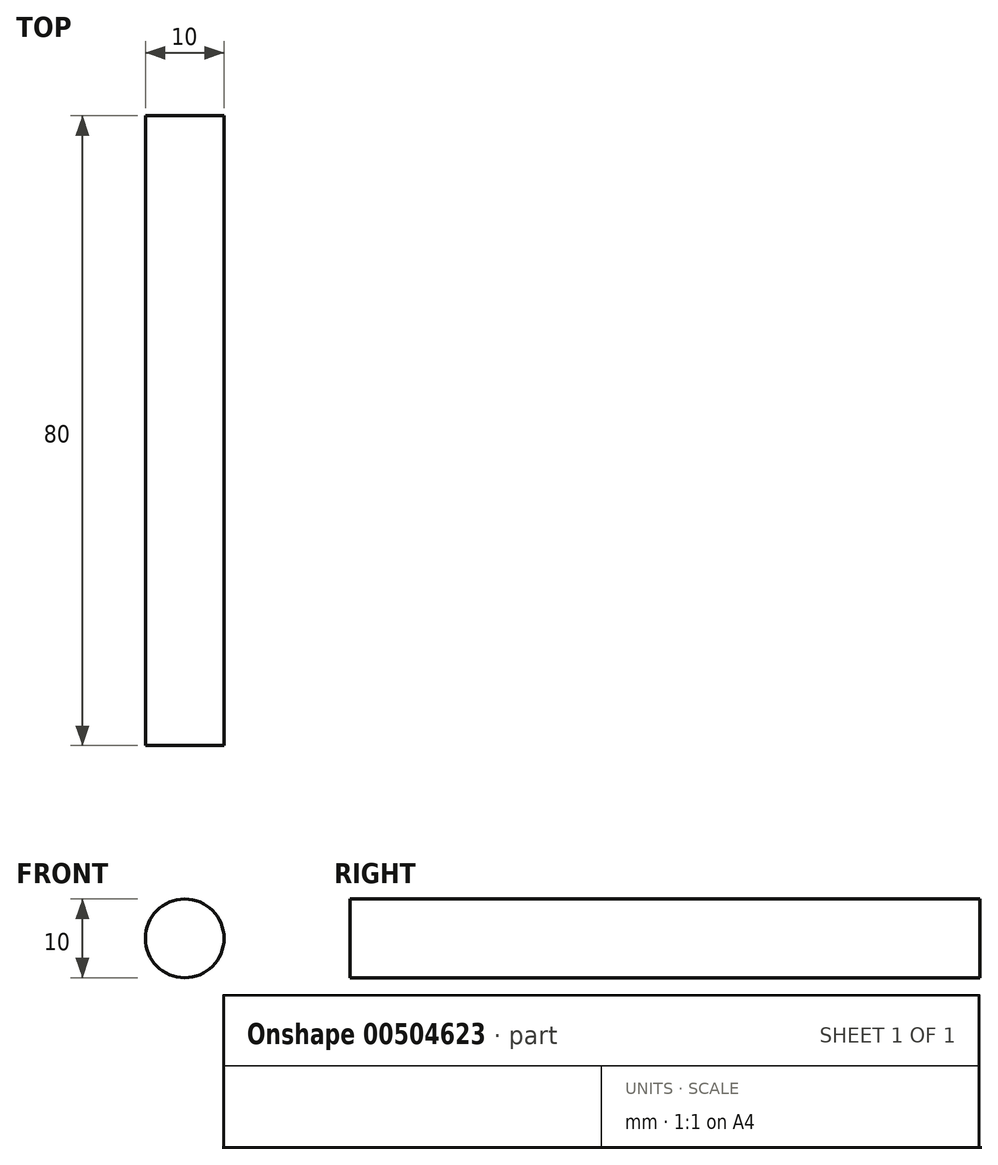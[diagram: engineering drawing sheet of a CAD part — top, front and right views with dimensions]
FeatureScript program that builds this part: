
annotation { "Feature Type Name" : "Feature", "Feature Type Description" : "" }
export const myFeature = defineFeature(function(context is Context, id is Id, definition is map)
    precondition{}
    {
        {
            var Q0;
            Q0=qCreatedBy(makeId("Front.planeOp"),FACE);
            var sketch = newSketch(context, id + "F0", { "sketchPlane" : qUnion([Q0])});
            skCircle(sketch, "E0", {"center": v(0, 0) * mm, "radius": 5 * mm});
            skLineSegment(sketch, "E1", {"start": v(0, 0) * mm, "end": v(5, 0) * mm});
            skSolve(sketch);
        }
        {
            var Q0;
            Q0=qSketchRegion(id+"F0",true);
            extrude(context, id + "F1", {"entities" : qUnion([Q0]), "depth" : 40 * mm, "hasSecondDirection" : true, "secondDirectionOppositeDirection" : true, "secondDirectionDepth" : 40 * mm, "offsetDistance" : 25 * mm});
        }
    });
